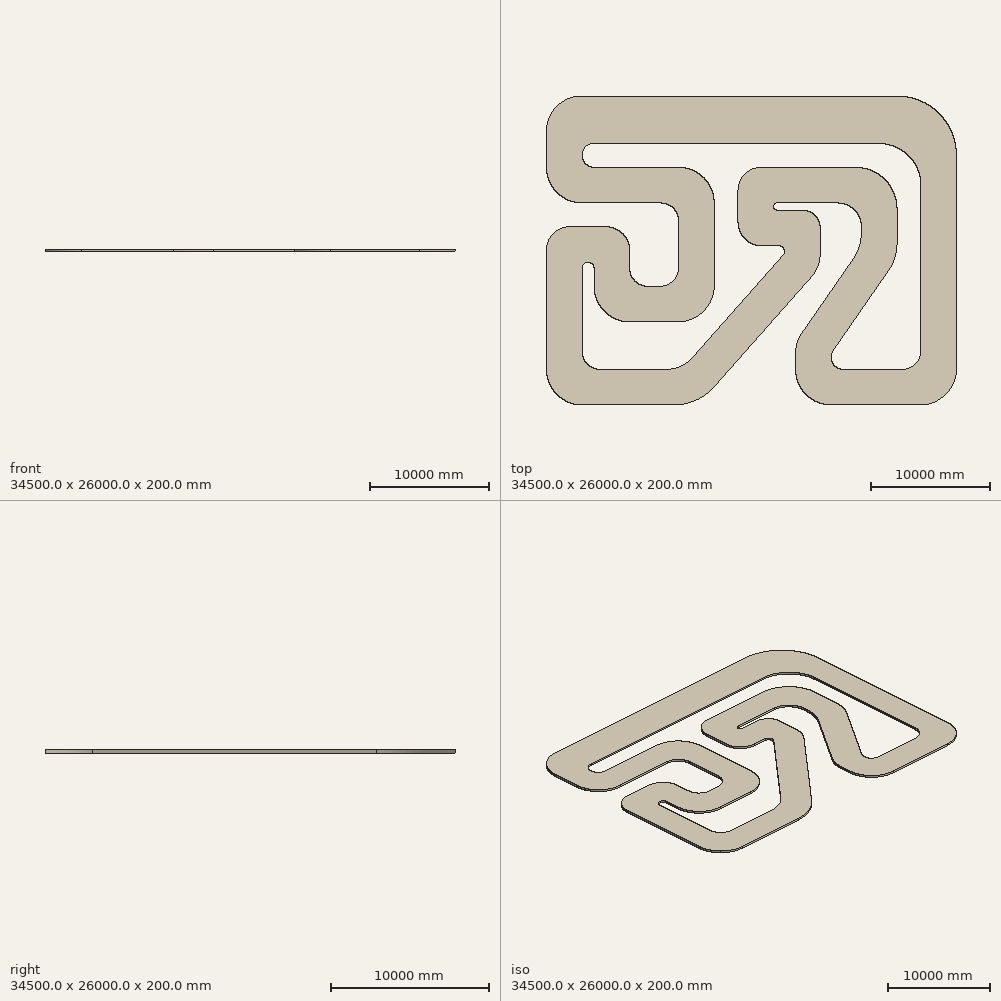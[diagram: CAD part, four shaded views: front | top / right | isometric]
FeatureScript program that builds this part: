
annotation { "Feature Type Name" : "Feature", "Feature Type Description" : "" }
export const myFeature = defineFeature(function(context is Context, id is Id, definition is map)
    precondition{}
    {
        {
            var Q0;
            Q0=qCreatedBy(makeId("Top.planeOp"),FACE);
            var sketch = newSketch(context, id + "F0", { "sketchPlane" : qUnion([Q0])});
            skLineSegment(sketch, "E0.bottom", {"start": v(-20929.36, 17336.87) * mm, "end": v(16070.64, 17336.87) * mm});
            skLineSegment(sketch, "E0.top", {"start": v(-20929.36, -11663.13) * mm, "end": v(16070.64, -11663.13) * mm});
            skLineSegment(sketch, "E0.left", {"start": v(-20929.36, 17336.87) * mm, "end": v(-20929.36, -11663.13) * mm});
            skLineSegment(sketch, "E0.right", {"start": v(16070.64, 17336.87) * mm, "end": v(16070.64, -11663.13) * mm});
            skLineSegment(sketch, "E1.bottom", {"start": v(-16929.36, 16336.87) * mm, "end": v(9570.64, 16336.87) * mm});
            skLineSegment(sketch, "E1.top", {"start": v(4032.57, -9663.13) * mm, "end": v(11570.64, -9663.13) * mm});
            skLineSegment(sketch, "E1.left", {"start": v(-19929.36, 3336.87) * mm, "end": v(-19929.36, -6663.13) * mm});
            skLineSegment(sketch, "E1.right", {"start": v(14570.64, 11336.87) * mm, "end": v(14570.64, -6663.13) * mm});
            skLineSegment(sketch, "E2", {"start": v(-15929.36, 12336.87) * mm, "end": v(8070.64, 12336.87) * mm});
            skLineSegment(sketch, "E3", {"start": v(11570.64, 8836.87) * mm, "end": v(11570.64, -5163.13) * mm});
            skPoint(sketch, "E4.visualSharp", {"position": v(11570.64, 12336.87) * mm});
            skArc(sketch, "E4.filletArc", {"start": v(11570.64, 8836.87) * mm, "mid": v(10545.52, 11311.74) * mm, "end": v(8070.64, 12336.87) * mm});
            skLineSegment(sketch, "E5", {"start": v(9570.64, 3898.2) * mm, "end": v(9570.64, 6836.87) * mm});
            skLineSegment(sketch, "E6", {"start": v(6070.64, 10336.87) * mm, "end": v(-1815.66, 10336.87) * mm});
            skLineSegment(sketch, "E7", {"start": v(10070.64, -6663.13) * mm, "end": v(5032.57, -6663.13) * mm});
            skLineSegment(sketch, "E8", {"start": v(4210.38, -5093.92) * mm, "end": v(8859.41, 1621.36) * mm});
            skLineSegment(sketch, "E9", {"start": v(1566, -3643.13) * mm, "end": v(5859.41, 2558.49) * mm});
            skLineSegment(sketch, "E10", {"start": v(6570.64, 5336.87) * mm, "end": v(6570.64, 4835.33) * mm});
            skLineSegment(sketch, "E11", {"start": v(4570.64, 7336.87) * mm, "end": v(-515.66, 7336.87) * mm});
            skLineSegment(sketch, "E12", {"start": v(1032.57, -5350.76) * mm, "end": v(1032.57, -6663.13) * mm});
            skLineSegment(sketch, "E13", {"start": v(-815.66, 7036.87) * mm, "end": v(-815.66, 7036.87) * mm});
            skLineSegment(sketch, "E14", {"start": v(-515.66, 6736.87) * mm, "end": v(1603.98, 6736.87) * mm});
            skLineSegment(sketch, "E15", {"start": v(3103.98, 5236.87) * mm, "end": v(3103.98, 3047.44) * mm});
            skLineSegment(sketch, "E16", {"start": v(2350.91, 1059.66) * mm, "end": v(-5791.96, -8144.8) * mm});
            skLineSegment(sketch, "E17", {"start": v(-16929.36, 11336.87) * mm, "end": v(-16929.36, 11336.87) * mm});
            skLineSegment(sketch, "E18", {"start": v(-3815.66, 8336.87) * mm, "end": v(-3815.66, 5736.87) * mm});
            skLineSegment(sketch, "E19", {"start": v(-1815.66, 3736.87) * mm, "end": v(-396.02, 3736.87) * mm});
            skLineSegment(sketch, "E20", {"start": v(-21.53, 2905.57) * mm, "end": v(-7591.16, -5650.92) * mm});
            skLineSegment(sketch, "E21", {"start": v(-9838.09, -6663.13) * mm, "end": v(-15429.36, -6663.13) * mm});
            skLineSegment(sketch, "E22", {"start": v(-16929.36, -5163.13) * mm, "end": v(-16929.36, 1836.87) * mm});
            skLineSegment(sketch, "E23", {"start": v(-5815.66, 331.03) * mm, "end": v(-5815.66, 7336.87) * mm});
            skLineSegment(sketch, "E24", {"start": v(-17929.36, 5336.87) * mm, "end": v(-14929.66, 5336.87) * mm});
            skLineSegment(sketch, "E25", {"start": v(-12929.66, 3336.87) * mm, "end": v(-12929.66, 1831.03) * mm});
            skLineSegment(sketch, "E26", {"start": v(-11429.66, 331.03) * mm, "end": v(-10315.66, 331.03) * mm});
            skLineSegment(sketch, "E27", {"start": v(-8815.66, 1831.03) * mm, "end": v(-8815.66, 5836.87) * mm});
            skLineSegment(sketch, "E28", {"start": v(-10315.66, 7336.87) * mm, "end": v(-16929.36, 7336.87) * mm});
            skPoint(sketch, "E29.visualSharp", {"position": v(9570.64, 10336.87) * mm});
            skArc(sketch, "E29.filletArc", {"start": v(9570.64, 6836.87) * mm, "mid": v(8545.52, 9311.74) * mm, "end": v(6070.64, 10336.87) * mm});
            skArc(sketch, "E30.filletArc", {"start": v(-1815.66, 10336.87) * mm, "mid": v(-3229.88, 9751.08) * mm, "end": v(-3815.66, 8336.87) * mm});
            skPoint(sketch, "E31.visualSharp", {"position": v(-3815.66, 3736.87) * mm});
            skArc(sketch, "E31.filletArc", {"start": v(-3815.66, 5736.87) * mm, "mid": v(-3229.88, 4322.65) * mm, "end": v(-1815.66, 3736.87) * mm});
            skArc(sketch, "E32.filletArc", {"start": v(-17929.36, 5336.87) * mm, "mid": v(-19343.57, 4751.08) * mm, "end": v(-19929.36, 3336.87) * mm});
            skPoint(sketch, "E33.visualSharp", {"position": v(-19929.36, -9663.13) * mm});
            skArc(sketch, "E33.filletArc", {"start": v(-19929.36, -6663.13) * mm, "mid": v(-19050.68, -8784.45) * mm, "end": v(-16929.36, -9663.13) * mm});
            skPoint(sketch, "E34.visualSharp", {"position": v(14570.64, -9663.13) * mm});
            skArc(sketch, "E34.filletArc", {"start": v(11570.64, -9663.13) * mm, "mid": v(13691.96, -8784.45) * mm, "end": v(14570.64, -6663.13) * mm});
            skArc(sketch, "E35.filletArc", {"start": v(1032.57, -6663.13) * mm, "mid": v(1911.25, -8784.45) * mm, "end": v(4032.57, -9663.13) * mm});
            skLineSegment(sketch, "E36", {"start": v(-9162.36, -9663.13) * mm, "end": v(-16929.36, -9663.13) * mm});
            skLineSegment(sketch, "E37", {"start": v(-19929.36, 13336.87) * mm, "end": v(-19929.36, 10336.87) * mm});
            skLineSegment(sketch, "E38", {"start": v(-15929.36, 10336.87) * mm, "end": v(-8815.66, 10336.87) * mm});
            skPoint(sketch, "E39.visualSharp", {"position": v(-19929.36, 16336.87) * mm});
            skArc(sketch, "E39.filletArc", {"start": v(-16929.36, 16336.87) * mm, "mid": v(-19050.68, 15458.19) * mm, "end": v(-19929.36, 13336.87) * mm});
            skPoint(sketch, "E40.visualSharp", {"position": v(-19929.36, 7336.87) * mm});
            skArc(sketch, "E40.filletArc", {"start": v(-19929.36, 10336.87) * mm, "mid": v(-19050.68, 8215.55) * mm, "end": v(-16929.36, 7336.87) * mm});
            skPoint(sketch, "E41.visualSharp", {"position": v(14570.64, 16336.87) * mm});
            skArc(sketch, "E41.filletArc", {"start": v(14570.64, 11336.87) * mm, "mid": v(13106.18, 14872.4) * mm, "end": v(9570.64, 16336.87) * mm});
            skArc(sketch, "E42.filletArc", {"start": v(-16929.36, 11336.87) * mm, "mid": v(-16636.46, 10629.76) * mm, "end": v(-15929.36, 10336.87) * mm});
            skPoint(sketch, "E43.visualSharp", {"position": v(-16929.36, 12336.87) * mm});
            skArc(sketch, "E43.filletArc", {"start": v(-15929.36, 12336.87) * mm, "mid": v(-16636.46, 12043.97) * mm, "end": v(-16929.36, 11336.87) * mm});
            skPoint(sketch, "E44.visualSharp", {"position": v(-5815.66, 10336.87) * mm});
            skArc(sketch, "E44.filletArc", {"start": v(-5815.66, 7336.87) * mm, "mid": v(-6694.34, 9458.19) * mm, "end": v(-8815.66, 10336.87) * mm});
            skPoint(sketch, "E45.visualSharp", {"position": v(3124, -6663.13) * mm});
            skArc(sketch, "E45.filletArc", {"start": v(4210.38, -5093.92) * mm, "mid": v(4146.79, -6127.24) * mm, "end": v(5032.57, -6663.13) * mm});
            skArc(sketch, "E46.filletArc", {"start": v(10070.64, -6663.13) * mm, "mid": v(11131.3, -6223.8) * mm, "end": v(11570.64, -5163.13) * mm});
            skPoint(sketch, "E47.visualSharp", {"position": v(-16929.36, 30181.47) * mm});
            skArc(sketch, "E47.filletArc", {"start": v(-15929.66, 1854.31) * mm, "mid": v(-16438.08, 2336.8) * mm, "end": v(-16929.36, 1836.87) * mm});
            skPoint(sketch, "E48.visualSharp", {"position": v(-12929.66, 331.03) * mm});
            skArc(sketch, "E48.filletArc", {"start": v(-12929.66, 1831.03) * mm, "mid": v(-12490.32, 770.37) * mm, "end": v(-11429.66, 331.03) * mm});
            skArc(sketch, "E49.filletArc", {"start": v(-10315.66, 331.03) * mm, "mid": v(-9255, 770.37) * mm, "end": v(-8815.66, 1831.03) * mm});
            skArc(sketch, "E50.filletArc", {"start": v(-8815.66, 5836.87) * mm, "mid": v(-9255, 6897.53) * mm, "end": v(-10315.66, 7336.87) * mm});
            skPoint(sketch, "E51.visualSharp", {"position": v(-12929.66, 5336.87) * mm});
            skArc(sketch, "E51.filletArc", {"start": v(-12929.66, 3336.87) * mm, "mid": v(-13515.45, 4751.08) * mm, "end": v(-14929.66, 5336.87) * mm});
            skArc(sketch, "E52.filletArc", {"start": v(-16929.36, -5163.13) * mm, "mid": v(-16490.02, -6223.8) * mm, "end": v(-15429.36, -6663.13) * mm});
            skPoint(sketch, "E53.visualSharp", {"position": v(-8486.63, -6663.13) * mm});
            skArc(sketch, "E53.filletArc", {"start": v(-9838.09, -6663.13) * mm, "mid": v(-8605.89, -6398.4) * mm, "end": v(-7591.16, -5650.92) * mm});
            skPoint(sketch, "E54.visualSharp", {"position": v(6570.64, 3585.82) * mm});
            skArc(sketch, "E54.filletArc", {"start": v(5859.41, 2558.49) * mm, "mid": v(6388.7, 3642.66) * mm, "end": v(6570.64, 4835.33) * mm});
            skPoint(sketch, "E55.visualSharp", {"position": v(6570.64, 7336.87) * mm});
            skArc(sketch, "E55.filletArc", {"start": v(6570.64, 5336.87) * mm, "mid": v(5984.86, 6751.08) * mm, "end": v(4570.64, 7336.87) * mm});
            skPoint(sketch, "E56.visualSharp", {"position": v(3103.98, 1910.9) * mm});
            skArc(sketch, "E56.filletArc", {"start": v(2350.91, 1059.66) * mm, "mid": v(2909.4, 1984.62) * mm, "end": v(3103.98, 3047.44) * mm});
            skPoint(sketch, "E57.visualSharp", {"position": v(3103.98, 6736.87) * mm});
            skArc(sketch, "E57.filletArc", {"start": v(3103.98, 5236.87) * mm, "mid": v(2664.64, 6297.53) * mm, "end": v(1603.98, 6736.87) * mm});
            skPoint(sketch, "E58.visualSharp", {"position": v(713.89, 3736.87) * mm});
            skArc(sketch, "E58.filletArc", {"start": v(-21.53, 2905.57) * mm, "mid": v(59.86, 3442.24) * mm, "end": v(-396.02, 3736.87) * mm});
            skPoint(sketch, "E59.visualSharp", {"position": v(-7135.16, -9663.13) * mm});
            skArc(sketch, "E59.filletArc", {"start": v(-9162.36, -9663.13) * mm, "mid": v(-7314.05, -9266.03) * mm, "end": v(-5791.96, -8144.8) * mm});
            skPoint(sketch, "E60.visualSharp", {"position": v(9570.64, 2648.7) * mm});
            skArc(sketch, "E60.filletArc", {"start": v(8859.41, 1621.36) * mm, "mid": v(9388.7, 2705.53) * mm, "end": v(9570.64, 3898.2) * mm});
            skPoint(sketch, "E61.visualSharp", {"position": v(-815.66, 7336.87) * mm});
            skArc(sketch, "E61.filletArc", {"start": v(-515.66, 7336.87) * mm, "mid": v(-727.8, 7249) * mm, "end": v(-815.66, 7036.87) * mm});
            skPoint(sketch, "E62.visualSharp", {"position": v(-815.66, 6736.87) * mm});
            skArc(sketch, "E62.filletArc", {"start": v(-815.66, 7036.87) * mm, "mid": v(-727.8, 6824.74) * mm, "end": v(-515.66, 6736.87) * mm});
            skLineSegment(sketch, "E63", {"start": v(-12929.66, -2668.97) * mm, "end": v(-8815.66, -2668.97) * mm});
            skPoint(sketch, "E64.visualSharp", {"position": v(1032.57, -4413.63) * mm});
            skArc(sketch, "E64.filletArc", {"start": v(1566, -3643.13) * mm, "mid": v(1169.03, -4456.25) * mm, "end": v(1032.57, -5350.76) * mm});
            skLineSegment(sketch, "E65", {"start": v(-15929.66, 1854.31) * mm, "end": v(-15929.66, 331.03) * mm});
            skPoint(sketch, "E66.visualSharp", {"position": v(-15929.66, -2668.97) * mm});
            skArc(sketch, "E66.filletArc", {"start": v(-15929.66, 331.03) * mm, "mid": v(-15050.98, -1790.29) * mm, "end": v(-12929.66, -2668.97) * mm});
            skPoint(sketch, "E67.visualSharp", {"position": v(-5815.66, -2668.97) * mm});
            skArc(sketch, "E67.filletArc", {"start": v(-8815.66, -2668.97) * mm, "mid": v(-6694.34, -1790.29) * mm, "end": v(-5815.66, 331.03) * mm});
            skSolve(sketch);
        }
        {
            var Q0;
            Q0=makeQuery(id+"F0.imprint","IMPRINT",FACE,{"disambiguationData":[TD([[makeQuery(id+"F0.imprint","IMPRINT",EDGE,{"derivedFrom":sQuery(id+"F0.wireOp",EDGE,"E1.bottom")}),-1.0]])]});
            extrude(context, id + "F1", {"entities" : qUnion([Q0]), "depth" : 200 * mm, "offsetDistance" : 25 * mm});
        }
    });
